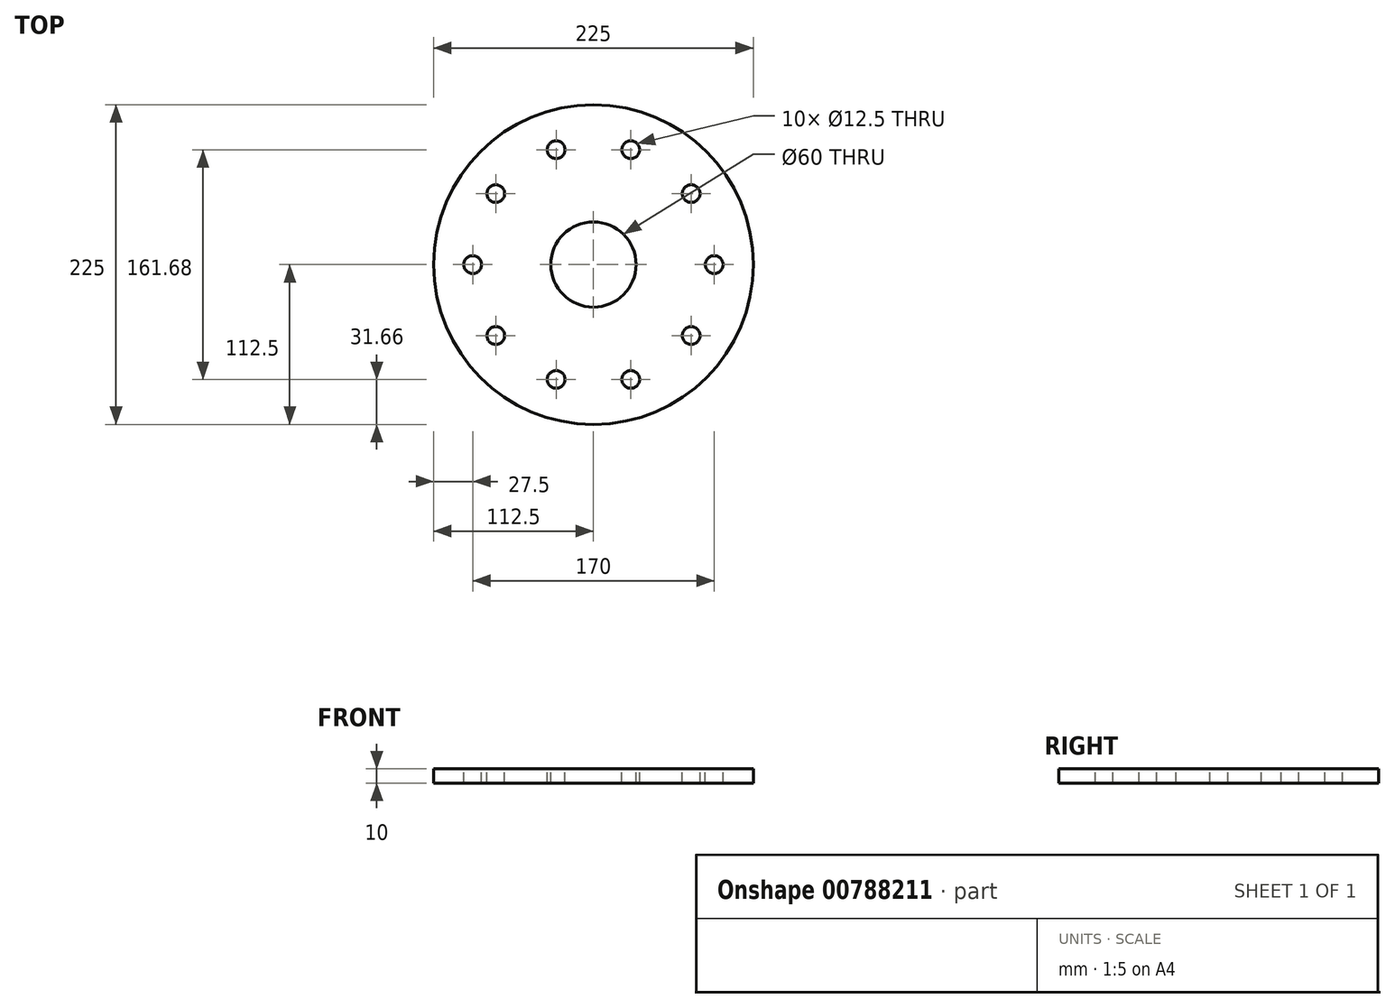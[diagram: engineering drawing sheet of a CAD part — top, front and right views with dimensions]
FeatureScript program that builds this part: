
annotation { "Feature Type Name" : "Feature", "Feature Type Description" : "" }
export const myFeature = defineFeature(function(context is Context, id is Id, definition is map)
    precondition{}
    {
        {
            var Q0;
            Q0=qCreatedBy(makeId("Top.planeOp"),FACE);
            var sketch = newSketch(context, id + "F0", { "sketchPlane" : qUnion([Q0])});
            skCircle(sketch, "E0", {"center": v(0, 0) * mm, "radius": 112.5 * mm});
            skSolve(sketch);
        }
        {
            var Q0;
            Q0 = qSketchRegion(id + "F0", true);
            extrude(context, id + "F1", {"entities" : qUnion([Q0]), "depth" : 10 * mm, "offsetDistance" : 25 * mm});
        }
        {
            var Q0;
            Q0=makeQuery(id+"F1.opExtrude","CAP_FACE",FACE,{"disambiguationData":[OSD([sQuery(id+"F0.wireOp",EDGE,"E0")])],"isStart":false});
            var sketch = newSketch(context, id + "F2", { "sketchPlane" : qUnion([Q0])});
            skCircle(sketch, "E1", {"center": v(0, 0) * mm, "radius": 30 * mm});
            skSolve(sketch);
        }
        {
            var Q0;
            Q0 = qSketchRegion(id + "F2", true);
            extrude(context, id + "F3", {"entities" : qUnion([Q0]), "operationType" : NewBodyOperationType.REMOVE, "endBound" : BoundingType.UP_TO_NEXT, "oppositeDirection" : true, "depth" : 25 * mm, "offsetDistance" : 25 * mm});
        }
        {
            var Q0;
            Q0=makeQuery(id+"F1.opExtrude","CAP_FACE",FACE,{"disambiguationData":[OSD([sQuery(id+"F0.wireOp",EDGE,"E0")])],"isStart":false});
            var sketch = newSketch(context, id + "F4", { "sketchPlane" : qUnion([Q0])});
            skPoint(sketch, "E2", {"position": v(85, 0) * mm});
            skPoint(sketch, "E3.1.0", {"position": v(68.77, 49.96) * mm});
            skPoint(sketch, "E3.2.0", {"position": v(26.27, 80.84) * mm});
            skPoint(sketch, "E3.3.0", {"position": v(-26.27, 80.84) * mm});
            skPoint(sketch, "E3.4.0", {"position": v(-68.77, 49.96) * mm});
            skPoint(sketch, "E3.5.0", {"position": v(-85, 0) * mm});
            skPoint(sketch, "E3.6.0", {"position": v(-68.77, -49.96) * mm});
            skPoint(sketch, "E3.7.0", {"position": v(-26.27, -80.84) * mm});
            skPoint(sketch, "E3.8.0", {"position": v(26.27, -80.84) * mm});
            skPoint(sketch, "E3.9.0", {"position": v(68.77, -49.96) * mm});
            skSolve(sketch);
        }
        {
            var Q0;
            Q0=sQuery(id+"F4.wireOp",VERTEX,"E2");
            var Q1;
            Q1=sQuery(id+"F4.wireOp",VERTEX,"E3.9.0");
            var Q2;
            Q2=sQuery(id+"F4.wireOp",VERTEX,"E3.1.0");
            var Q3;
            Q3=sQuery(id+"F4.wireOp",VERTEX,"E3.2.0");
            var Q4;
            Q4=sQuery(id+"F4.wireOp",VERTEX,"E3.3.0");
            var Q5;
            Q5=sQuery(id+"F4.wireOp",VERTEX,"E3.4.0");
            var Q6;
            Q6=sQuery(id+"F4.wireOp",VERTEX,"E3.5.0");
            var Q7;
            Q7=sQuery(id+"F4.wireOp",VERTEX,"E3.6.0");
            var Q8;
            Q8=sQuery(id+"F4.wireOp",VERTEX,"E3.7.0");
            var Q9;
            Q9=sQuery(id+"F4.wireOp",VERTEX,"E3.8.0");
            var Q10;
            Q10=makeQuery(id+"F1.opExtrude","SWEPT_BODY",BODY,{"disambiguationData":[OSD([sQuery(id+"F0.wireOp",EDGE,"E0")])]});
            hole(context, id + "F5", {"style" : HoleStyle.SIMPLE, "endStyle" : HoleEndStyle.THROUGH, "holeDiameter" : 12.5 * mm, "majorDiameter" : 5 * mm, "isTappedThrough" : true, "tappedDepth" : 12 * mm, "tapClearance" : 3, "locations" : qUnion([Q0, Q1, Q2, Q3, Q4, Q5, Q6, Q7, Q8, Q9]), "scope" : qUnion([Q10])});
        }
    });
